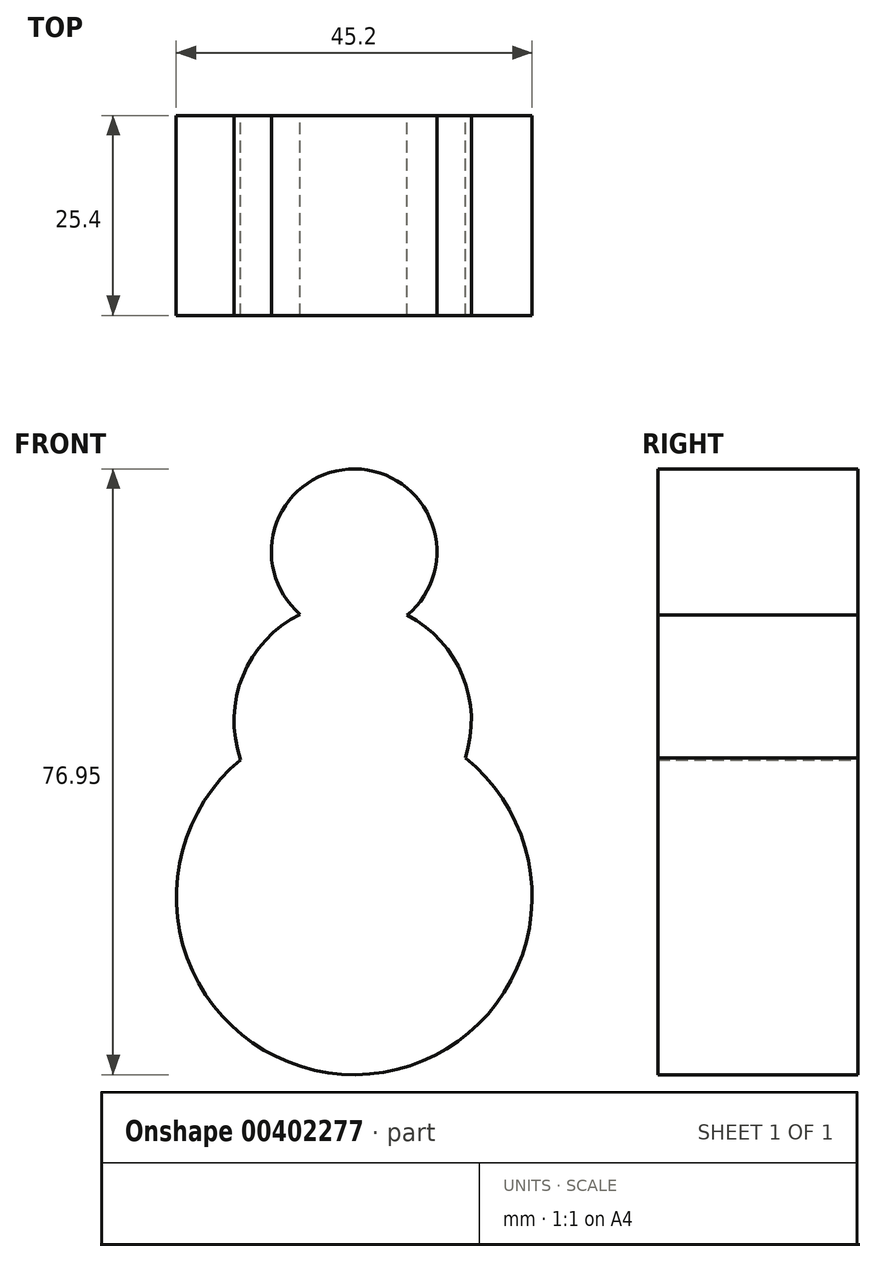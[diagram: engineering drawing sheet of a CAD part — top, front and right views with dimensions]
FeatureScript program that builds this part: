
annotation { "Feature Type Name" : "Feature", "Feature Type Description" : "" }
export const myFeature = defineFeature(function(context is Context, id is Id, definition is map)
    precondition{}
    {
        {
            var Q0;
            Q0=qCreatedBy(makeId("Front.planeOp"),FACE);
            var sketch = newSketch(context, id + "F0", { "sketchPlane" : qUnion([Q0])});
            skCircle(sketch, "E0", {"center": v(0, -53.56) * mm, "radius": 22.6 * mm});
            skArc(sketch, "E1", {"start": v(14.12, -35.91) * mm, "mid": v(-0.3, -16.1) * mm, "end": v(-14.4, -36.15) * mm});
            skArc(sketch, "E2", {"start": v(6.74, -17.78) * mm, "mid": v(0.1, 0.8) * mm, "end": v(-6.87, -17.67) * mm});
            skPoint(sketch, "E3", {"position": v(-4.8, -4.72) * mm});
            skPoint(sketch, "E4", {"position": v(3.51, -4.72) * mm});
            skPoint(sketch, "E5", {"position": v(0, -18.78) * mm});
            skPoint(sketch, "E6", {"position": v(0, -22.85) * mm});
            skPoint(sketch, "E7", {"position": v(0, -27.84) * mm});
            skLineSegment(sketch, "E8", {"start": v(-12.22, -22.1) * mm, "end": v(-29.23, -28.95) * mm});
            skLineSegment(sketch, "E9", {"start": v(-29.23, -28.95) * mm, "end": v(-29.23, -34.32) * mm});
            skLineSegment(sketch, "E10", {"start": v(-29.23, -28.95) * mm, "end": v(-33.48, -33.2) * mm});
            skLineSegment(sketch, "E11", {"start": v(-29.23, -28.95) * mm, "end": v(-34.96, -28.95) * mm});
            skLineSegment(sketch, "E12", {"start": v(12.71, -23.38) * mm, "end": v(29.74, -30.2) * mm});
            skLineSegment(sketch, "E13", {"start": v(29.74, -30.2) * mm, "end": v(29.74, -35.93) * mm});
            skLineSegment(sketch, "E14", {"start": v(29.74, -30.2) * mm, "end": v(34.64, -35.1) * mm});
            skLineSegment(sketch, "E15", {"start": v(29.74, -30.2) * mm, "end": v(36.21, -30.2) * mm});
            skLineSegment(sketch, "E16", {"start": v(0, -7.86) * mm, "end": v(8.5, -9.71) * mm});
            skLineSegment(sketch, "E17", {"start": v(8.5, -9.71) * mm, "end": v(0, -9.71) * mm});
            skArc(sketch, "E18", {"start": v(-2.96, -12.86) * mm, "mid": v(0.15, -15.07) * mm, "end": v(2.96, -12.49) * mm});
            skSolve(sketch);
        }
        {
            var Q0;
            {var subQ0=sQuery(id+"F0.wireOp",EDGE,"E2");Q0=makeQuery(id+"F0.imprint","IMPRINT",FACE,{"disambiguationData":[TD([[makeQuery(id+"F0.imprint","IMPRINT",EDGE,{"derivedFrom":subQ0}),1.0]])]});}
            var Q1;
            {var subQ1=sQuery(id+"F0.wireOp",EDGE,"E1");var subQ4=makeQuery(id+"F0.imprint","IMPRINT",VERTEX,{"disambiguationData":[OD(1.0)],"derivedFrom":subQ1});Q1=makeQuery(id+"F0.imprint","IMPRINT",FACE,{"disambiguationData":[TD([[makeQuery(id+"F0.imprint","IMPRINT",EDGE,{"disambiguationData":[TD([[subQ4,1.0]])],"derivedFrom":subQ1}),1.0]])]});}
            var Q2;
            {var subQ0=sQuery(id+"F0.wireOp",EDGE,"E1");var subQ1=sQuery(id+"F0.wireOp",EDGE,"E0");var subQ2=makeQuery(id+"F0.imprint","INTERSECT",VERTEX,{"disambiguationData":[OD(0.0)],"derivedFrom":[subQ1,subQ0]});Q2=makeQuery(id+"F0.imprint","IMPRINT",FACE,{"disambiguationData":[TD([[makeQuery(id+"F0.imprint","IMPRINT",EDGE,{"disambiguationData":[TD([[subQ2,-1.0]])],"derivedFrom":subQ1}),1.0]])]});}
            extrude(context, id + "F1", {"entities" : qUnion([Q0, Q1, Q2]), "depth" : 25.4 * mm});
        }
    });
